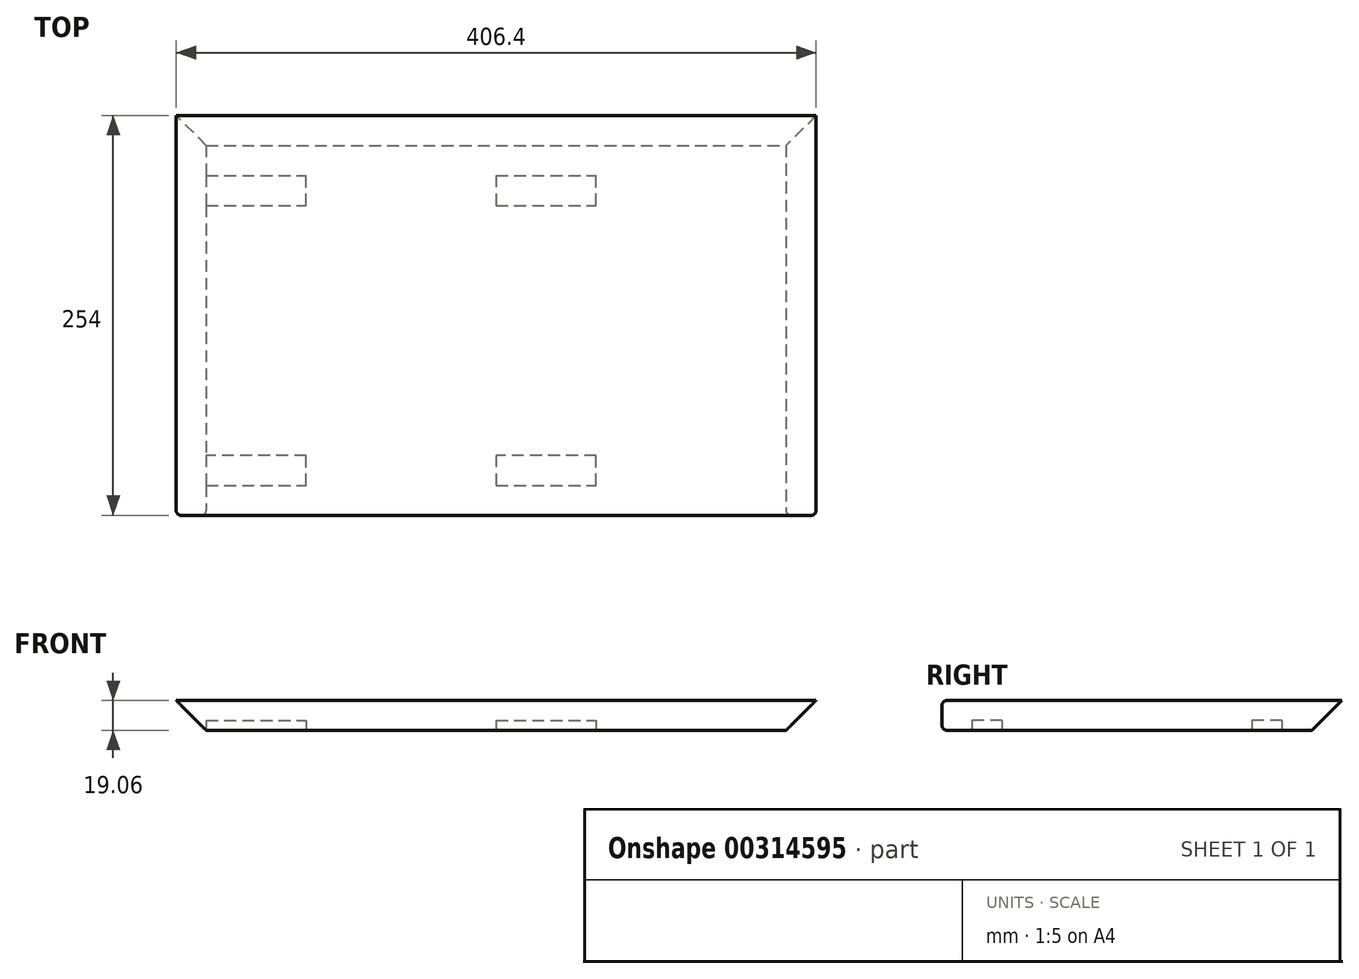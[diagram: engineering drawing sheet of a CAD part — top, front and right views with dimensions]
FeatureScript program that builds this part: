
annotation { "Feature Type Name" : "Feature", "Feature Type Description" : "" }
export const myFeature = defineFeature(function(context is Context, id is Id, definition is map)
    precondition{}
    {
        {
            var Q0;
            Q0=qCreatedBy(makeId("Front.planeOp"),FACE);
            var sketch = newSketch(context, id + "F0", { "sketchPlane" : qUnion([Q0])});
            skLineSegment(sketch, "E0", {"start": v(-203.2, 9.52) * mm, "end": v(203.2, 9.52) * mm});
            skLineSegment(sketch, "E1", {"start": v(203.2, 9.52) * mm, "end": v(184.15, -9.53) * mm});
            skLineSegment(sketch, "E2", {"start": v(184.15, -9.53) * mm, "end": v(-184.15, -9.53) * mm});
            skLineSegment(sketch, "E3", {"start": v(-184.15, -9.53) * mm, "end": v(-203.2, 9.53) * mm});
            skLineSegment(sketch, "E4", {"start": v(0, 9.53) * mm, "end": v(0, -9.53) * mm, "construction": true});
            skSolve(sketch);
        }
        {
            var Q0;
            Q0=qSketchRegion(id+"F0",true);
            extrude(context, id + "F1", {"entities" : qUnion([Q0]), "oppositeDirection" : true, "depth" : 254 * mm});
        }
        {
            var Q0;
            Q0=makeQuery(id+"F1.opExtrude","CAP_EDGE",EDGE,{"disambiguationData":[OSD([sQuery(id+"F0.wireOp",EDGE,"E2")])],"isStart":false});
            chamfer(context, id + "F2", {"entities" : qUnion([Q0]), "width" : 19.05 * mm, "tangentPropagation" : true});
        }
        {
            var Q0;
            Q0=makeQuery(id+"F1.opExtrude","SWEPT_FACE",FACE,{"disambiguationData":[OSD([sQuery(id+"F0.wireOp",EDGE,"E2")])]});
            var sketch = newSketch(context, id + "F3", { "sketchPlane" : qUnion([Q0])});
            skLineSegment(sketch, "E5", {"start": v(-184.15, -19.05) * mm, "end": v(184.15, -19.05) * mm});
            skLineSegment(sketch, "E6", {"start": v(184.15, -38.1) * mm, "end": v(-184.15, -38.1) * mm});
            skLineSegment(sketch, "E7", {"start": v(-184.15, -215.9) * mm, "end": v(184.15, -215.9) * mm});
            skLineSegment(sketch, "E8", {"start": v(-184.15, -196.85) * mm, "end": v(184.15, -196.85) * mm});
            skLineSegment(sketch, "E9", {"start": v(-120.65, 0) * mm, "end": v(-120.65, -234.95) * mm});
            skLineSegment(sketch, "E10", {"start": v(63.5, 0) * mm, "end": v(63.5, -234.95) * mm});
            skLineSegment(sketch, "E11", {"start": v(0, -234.95) * mm, "end": v(0, 0) * mm});
            skSolve(sketch);
        }
        {
            var Q0;
            {var subQ0=sQuery(id+"F3.wireOp",EDGE,"E5");var subQ3=sQuery(id+"F3.wireOp",EDGE,"E9");var subQ4=makeQuery(id+"F3.imprint","INTERSECT",VERTEX,{"derivedFrom":[subQ0,subQ3]});Q0=makeQuery(id+"F3.imprint","IMPRINT",FACE,{"disambiguationData":[TD([[makeQuery(id+"F3.imprint","IMPRINT",EDGE,{"disambiguationData":[TD([[subQ4,-1.0]])],"derivedFrom":subQ3}),-1.0]])]});}
            var Q1;
            {var subQ0=sQuery(id+"F3.wireOp",EDGE,"E11");var subQ1=sQuery(id+"F3.wireOp",EDGE,"E5");var subQ2=makeQuery(id+"F3.imprint","INTERSECT",VERTEX,{"derivedFrom":[subQ1,subQ0]});Q1=makeQuery(id+"F3.imprint","IMPRINT",FACE,{"disambiguationData":[TD([[makeQuery(id+"F3.imprint","IMPRINT",EDGE,{"disambiguationData":[TD([[subQ2,-1.0]])],"derivedFrom":subQ1}),-1.0]])]});}
            var Q2;
            {var subQ0=sQuery(id+"F3.wireOp",EDGE,"E11");var subQ1=sQuery(id+"F3.wireOp",EDGE,"E7");var subQ2=makeQuery(id+"F3.imprint","INTERSECT",VERTEX,{"derivedFrom":[subQ1,subQ0]});Q2=makeQuery(id+"F3.imprint","IMPRINT",FACE,{"disambiguationData":[TD([[makeQuery(id+"F3.imprint","IMPRINT",EDGE,{"disambiguationData":[TD([[subQ2,-1.0]])],"derivedFrom":subQ1}),1.0]])]});}
            var Q3;
            {var subQ0=sQuery(id+"F3.wireOp",EDGE,"E7");var subQ3=sQuery(id+"F3.wireOp",EDGE,"E9");var subQ4=makeQuery(id+"F3.imprint","INTERSECT",VERTEX,{"derivedFrom":[subQ0,subQ3]});Q3=makeQuery(id+"F3.imprint","IMPRINT",FACE,{"disambiguationData":[TD([[makeQuery(id+"F3.imprint","IMPRINT",EDGE,{"disambiguationData":[TD([[subQ4,1.0]])],"derivedFrom":subQ3}),-1.0]])]});}
            extrude(context, id + "F4", {"entities" : qUnion([Q0, Q1, Q2, Q3]), "operationType" : NewBodyOperationType.REMOVE, "oppositeDirection" : true, "depth" : 6.35 * mm});
        }
        {
            var Q0;
            Q0=makeQuery(id+"F1.opExtrude","CAP_EDGE",EDGE,{"disambiguationData":[OSD([sQuery(id+"F0.wireOp",EDGE,"E0")])],"isStart":true});
            var Q1;
            Q1=makeQuery(id+"F1.opExtrude","CAP_EDGE",EDGE,{"disambiguationData":[OSD([sQuery(id+"F0.wireOp",EDGE,"E2")])],"isStart":true});
            fillet(context, id + "F5", {"entities" : qUnion([Q0, Q1]), "radius" : 3.17 * mm, "tangentPropagation" : true, "allowEdgeOverflow" : false});
        }
    });
